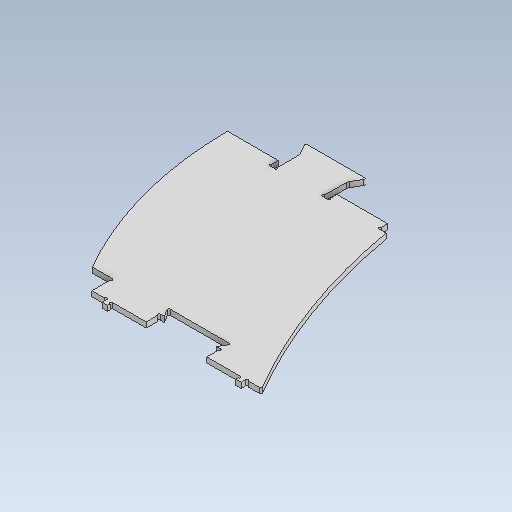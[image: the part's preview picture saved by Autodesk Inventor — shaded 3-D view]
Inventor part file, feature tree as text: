
AUTODESK INVENTOR PART (.ipt)
format: ipt  version: 2020 (Build 240168000, 168)  size: 278,528 bytes
history: native  units: mm
features: extrude x1, sketch x1
ambient origin geometry x8: Origin, YZ Plane, XZ Plane, XY Plane, X Axis, Y Axis, Z Axis, Center Point
bodies: Body1 (feature_tree)
feature tree (2):
  extrude  "Extrusion3"  Depth=1.333333mm
  sketch  "Sketch1"  dims[d99=181.29mm d102=2.666667mm d105=32.04mm d106=10.0mm d107=2.666667mm d108=6.5mm d109=2.666667mm d111=57.3335mm d120=6.0mm d121=0.0mm d127=9.666667mm d128=9.666667mm d129=1.333333mm d131=62.331193mm d132=1.333333mm d133=14.480979mm d134=1.333333mm d135=6.0mm d141=7.333333mm d142=5.0mm d145=1.333333mm d149=1.333333mm d151=658.71mm d152=5.0mm d153=68.568734mm d154=66.666667mm d155=1.333333mm d156=1.333333mm d158=1.333333mm d160=10.371579mm d161=10.371579mm d162=38.215633mm d163=38.235mm d164=15.668421mm d165=15.668421mm d166=23.333333mm d167=84.505753mm d169=264.866408mm d170=145.0381mm d171=6.000011mm d172=5.499681mm d173=1.333333mm d174=2.833339mm d175=145.000592mm]
